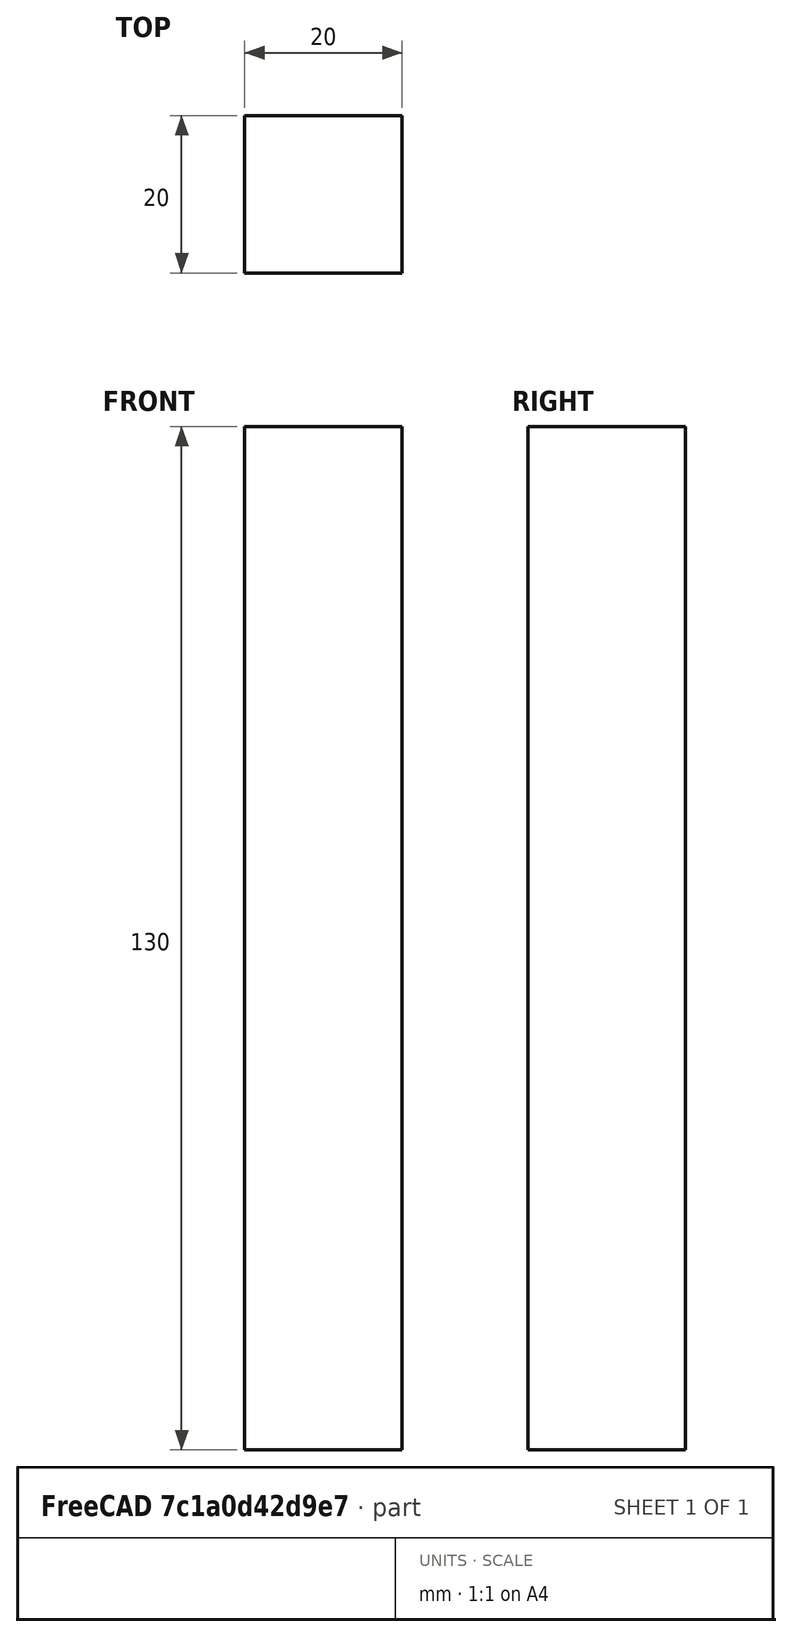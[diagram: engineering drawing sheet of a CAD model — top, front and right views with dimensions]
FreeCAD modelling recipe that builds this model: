
FCSTD DOCUMENT  (FreeCAD 0.19R24276 (Git))
Label: L130
License: All rights reserved
LicenseURL: http://en.wikipedia.org/wiki/All_rights_reserved
objects: Sketcher::SketchObject×1, PartDesign::Pad×1, PartDesign::Body×1
note: 4 computed .brp shape members not serialized (recipe doc carries the construction recipe); baked Part::Feature solids carry a one-line shape summary decoded from their .brp

FEATURE [Sketcher::SketchObject] Sketch
  FullyConstrained = true
  MapMode = 5
  Support = -> [XY_Plane]
  sketch-geometry (4):
    g0: LineSegment StartX=0 StartY=0 StartZ=0 EndX=20 EndY=0 EndZ=0
    g1: LineSegment StartX=20 StartY=0 StartZ=0 EndX=20 EndY=-20 EndZ=0
    g2: LineSegment StartX=20 StartY=-20 StartZ=0 EndX=0 EndY=-20 EndZ=0
    g3: LineSegment StartX=0 StartY=-20 StartZ=0 EndX=0 EndY=0 EndZ=0
  constraints (11):
    c: Coincident(g0,g1)
    c: Coincident(g1,g2)
    c: Coincident(g2,g3)
    c: Coincident(g3,g0)
    c: Horizontal(g0)
    c: Horizontal(g2)
    c: Vertical(g1)
    c: Vertical(g3)
    c: Coincident(g0,g-1)
    c: Equal(g1,g2)
    c: DistanceY(g1,g1) = 20
FEATURE [PartDesign::Pad] Pad
  Direction = (1,1,1)
  Length = 130
  Length2 = 100
  Profile = -> Sketch
  Type = 0
FEATURE [PartDesign::Body] Body
  Group = -> [Sketch,Pad]
  Origin = -> Origin
  Tip = -> Pad
